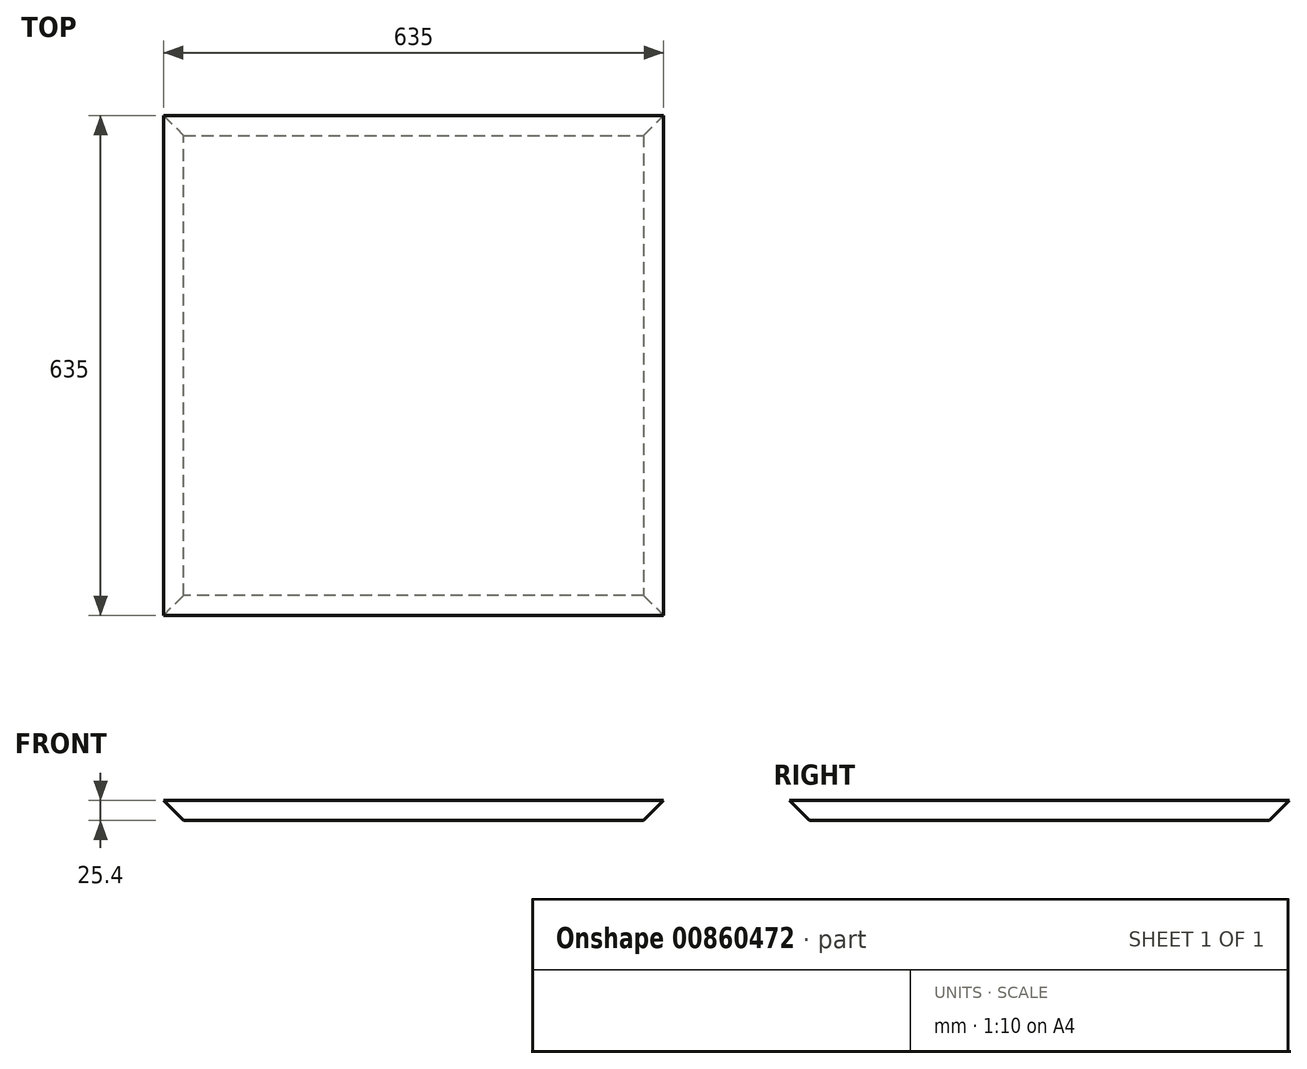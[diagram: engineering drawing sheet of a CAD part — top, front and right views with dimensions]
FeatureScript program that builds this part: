
annotation { "Feature Type Name" : "Feature", "Feature Type Description" : "" }
export const myFeature = defineFeature(function(context is Context, id is Id, definition is map)
    precondition{}
    {
        {
            var Q0;
            Q0=qCreatedBy(makeId("Top.planeOp"),FACE);
            var sketch = newSketch(context, id + "F0", { "sketchPlane" : qUnion([Q0])});
            skLineSegment(sketch, "E0.bottom", {"start": v(-317.5, 317.5) * mm, "end": v(317.5, 317.5) * mm});
            skLineSegment(sketch, "E0.top", {"start": v(-317.5, -317.5) * mm, "end": v(317.5, -317.5) * mm});
            skLineSegment(sketch, "E0.left", {"start": v(-317.5, 317.5) * mm, "end": v(-317.5, -317.5) * mm});
            skLineSegment(sketch, "E0.right", {"start": v(317.5, 317.5) * mm, "end": v(317.5, -317.5) * mm});
            skPoint(sketch, "E0.middle", {"position": v(0, 0) * mm});
            skSolve(sketch);
        }
        {
            var Q0;
            Q0 = qSketchRegion(id + "F0", true);
            extrude(context, id + "F1", {"entities" : qUnion([Q0]), "depth" : 25.4 * mm, "offsetDistance" : 25.4 * mm});
        }
        {
            var Q0;
            Q0=makeQuery(id+"F1.opExtrude","CAP_FACE",FACE,{"disambiguationData":[OSD([sQuery(id+"F0.wireOp",EDGE,"E0.bottom"),sQuery(id+"F0.wireOp",EDGE,"E0.top"),sQuery(id+"F0.wireOp",EDGE,"E0.left"),sQuery(id+"F0.wireOp",EDGE,"E0.right")])],"isStart":true});
            chamfer(context, id + "F2", {"entities" : qUnion([Q0]), "width" : 25.4 * mm, "tangentPropagation" : true});
        }
    });
